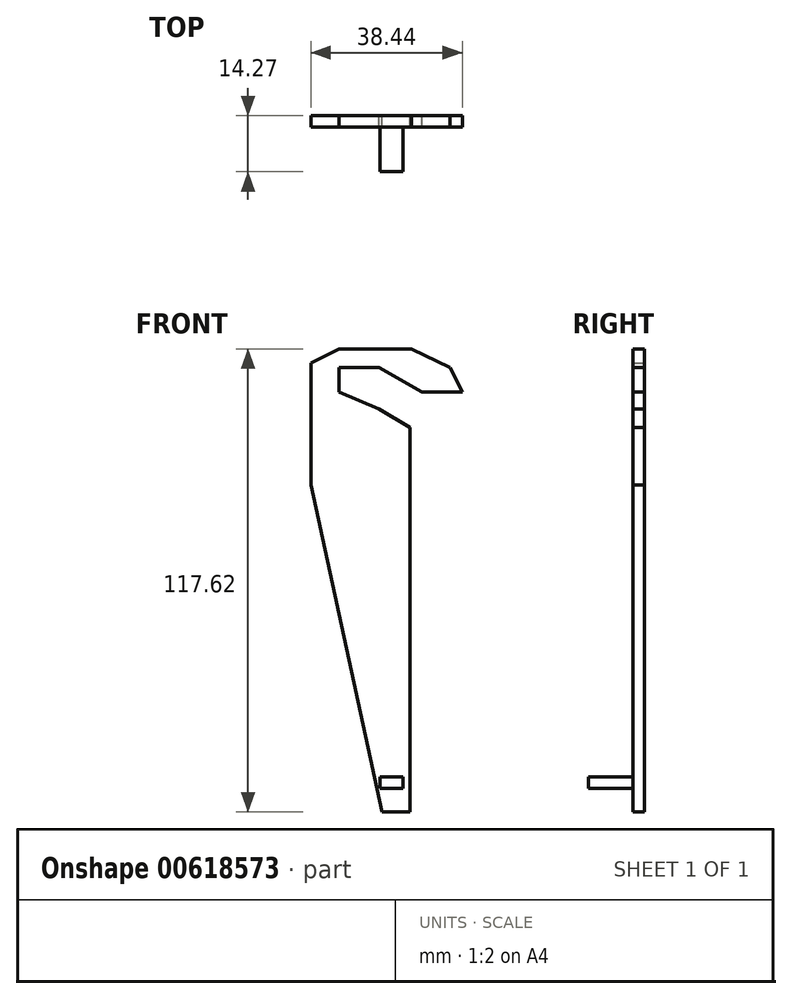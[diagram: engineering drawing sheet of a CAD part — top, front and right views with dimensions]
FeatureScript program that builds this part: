
annotation { "Feature Type Name" : "Feature", "Feature Type Description" : "" }
export const myFeature = defineFeature(function(context is Context, id is Id, definition is map)
    precondition{}
    {
        {
            var Q0;
            Q0=qCreatedBy(makeId("Front.planeOp"),FACE);
            var sketch = newSketch(context, id + "F0", { "sketchPlane" : qUnion([Q0])});
            skLineSegment(sketch, "E0.bottom", {"start": v(3.58, -41.5) * mm, "end": v(-3.59, -41.5) * mm});
            skLineSegment(sketch, "E0.top", {"start": v(3.59, 41.5) * mm, "end": v(-3.58, 41.5) * mm});
            skLineSegment(sketch, "E0.left", {"start": v(3.58, -41.5) * mm, "end": v(3.59, 41.5) * mm});
            skLineSegment(sketch, "E0.right", {"start": v(-3.59, -41.5) * mm, "end": v(-3.58, 41.5) * mm});
            skPoint(sketch, "E0.middle", {"position": v(0, 0) * mm});
            skLineSegment(sketch, "E1", {"start": v(3.59, 41.5) * mm, "end": v(-21.56, 41.5) * mm});
            skPoint(sketch, "E1.endSnap0", {"position": v(0, 41.5) * mm});
            skLineSegment(sketch, "E2", {"start": v(-21.56, 41.5) * mm, "end": v(-3.59, -41.5) * mm});
            skLineSegment(sketch, "E3.bottom", {"start": v(-21.56, 41.5) * mm, "end": v(3.56, 41.5) * mm});
            skLineSegment(sketch, "E3.top", {"start": v(-21.57, 56.15) * mm, "end": v(3.56, 56.15) * mm});
            skLineSegment(sketch, "E3.left", {"start": v(-21.56, 41.5) * mm, "end": v(-21.56, 56.15) * mm});
            skLineSegment(sketch, "E3.right", {"start": v(3.56, 41.5) * mm, "end": v(3.56, 56.15) * mm});
            skLineSegment(sketch, "E4", {"start": v(-21.56, 41.5) * mm, "end": v(-21.56, 72.5) * mm});
            skPoint(sketch, "E4.endSnap0", {"position": v(-21.56, 48.83) * mm});
            skLineSegment(sketch, "E5", {"start": v(-21.57, 72.5) * mm, "end": v(-14.4, 76.12) * mm});
            skLineSegment(sketch, "E6", {"start": v(-14.4, 76.12) * mm, "end": v(3.9, 76.12) * mm});
            skLineSegment(sketch, "E7", {"start": v(3.9, 76.12) * mm, "end": v(13.73, 71.36) * mm});
            skLineSegment(sketch, "E8", {"start": v(13.73, 71.36) * mm, "end": v(16.87, 65.13) * mm});
            skLineSegment(sketch, "E9", {"start": v(16.87, 65.13) * mm, "end": v(6.61, 65.13) * mm});
            skLineSegment(sketch, "E10", {"start": v(6.61, 65.13) * mm, "end": v(-4.24, 71.36) * mm});
            skLineSegment(sketch, "E11", {"start": v(-4.24, 71.36) * mm, "end": v(-14.4, 71.36) * mm});
            skLineSegment(sketch, "E12", {"start": v(-14.4, 71.36) * mm, "end": v(-14.4, 65.13) * mm});
            skLineSegment(sketch, "E13", {"start": v(-14.4, 65.13) * mm, "end": v(-4.24, 60.86) * mm});
            skLineSegment(sketch, "E14", {"start": v(-4.24, 60.86) * mm, "end": v(3.56, 56.15) * mm});
            skSolve(sketch);
        }
        {
            var Q0;
            {var subQ0=sQuery(id+"F0.wireOp",EDGE,"E0.right");Q0=makeQuery(id+"F0.imprint","IMPRINT",FACE,{"disambiguationData":[TD([[makeQuery(id+"F0.imprint","IMPRINT",EDGE,{"derivedFrom":subQ0}),1.0]])]});}
            var Q1;
            {var subQ1=sQuery(id+"F0.wireOp",EDGE,"E3.top");Q1=makeQuery(id+"F0.imprint","IMPRINT",FACE,{"disambiguationData":[TD([[makeQuery(id+"F0.imprint","IMPRINT",EDGE,{"derivedFrom":subQ1}),-1.0]])]});}
            var Q2;
            {var subQ0=sQuery(id+"F0.wireOp",EDGE,"E3.top");Q2=makeQuery(id+"F0.imprint","IMPRINT",FACE,{"disambiguationData":[TD([[makeQuery(id+"F0.imprint","IMPRINT",EDGE,{"derivedFrom":subQ0}),1.0]])]});}
            var Q3;
            Q3=makeQuery(id+"F0.imprint","IMPRINT",FACE,{"disambiguationData":[TD([[makeQuery(id+"F0.imprint","IMPRINT",EDGE,{"derivedFrom":sQuery(id+"F0.wireOp",EDGE,"E0.bottom")}),-1.0]])]});
            extrude(context, id + "F1", {"entities" : qUnion([Q0, Q1, Q2, Q3]), "depth" : 2.92 * mm, "offsetDistance" : 25.4 * mm});
        }
        {
            var Q0;
            Q0=qCreatedBy(makeId("Right.planeOp"),FACE);
            var sketch = newSketch(context, id + "F2", { "sketchPlane" : qUnion([Q0])});
            skLineSegment(sketch, "E15", {"start": v(-2.9, -35.57) * mm, "end": v(-14.27, -35.57) * mm});
            skLineSegment(sketch, "E16", {"start": v(-14.27, -35.57) * mm, "end": v(-14.27, -32.56) * mm});
            skLineSegment(sketch, "E17", {"start": v(-14.27, -32.56) * mm, "end": v(-2.9, -32.56) * mm});
            skLineSegment(sketch, "E18", {"start": v(-2.9, -32.56) * mm, "end": v(-2.9, -35.57) * mm});
            skSolve(sketch);
        }
        {
            var Q0;
            Q0=makeQuery(id+"F2.imprint","IMPRINT",FACE,{"disambiguationData":[TD([[makeQuery(id+"F2.imprint","IMPRINT",EDGE,{"derivedFrom":sQuery(id+"F2.wireOp",EDGE,"E15")}),-1.0]])]});
            extrude(context, id + "F3", {"entities" : qUnion([Q0]), "operationType" : NewBodyOperationType.ADD, "oppositeDirection" : true, "depth" : 4.06 * mm, "offsetDistance" : 25.4 * mm, "hasSecondDirection" : true, "secondDirectionOppositeDirection" : false, "secondDirectionDepth" : 1.78 * mm});
        }
    });
